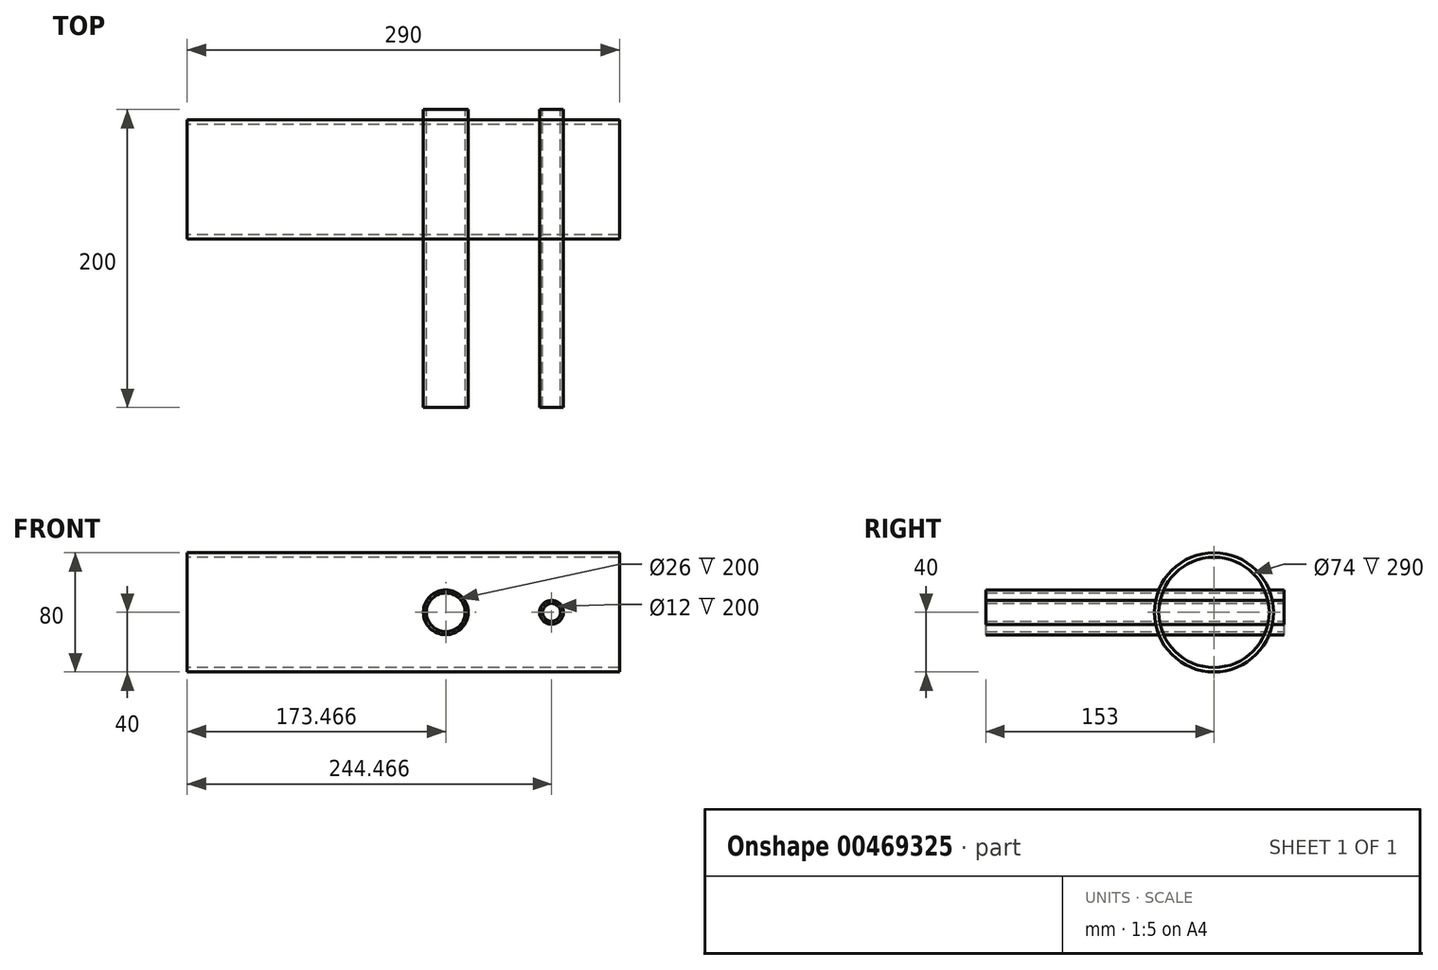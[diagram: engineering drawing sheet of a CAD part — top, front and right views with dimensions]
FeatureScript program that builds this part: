
annotation { "Feature Type Name" : "Feature", "Feature Type Description" : "" }
export const myFeature = defineFeature(function(context is Context, id is Id, definition is map)
    precondition{}
    {
        {
            var Q0;
            Q0=qCreatedBy(makeId("Top.planeOp"),FACE);
            var sketch = newSketch(context, id + "F0", { "sketchPlane" : qUnion([Q0])});
            skLineSegment(sketch, "E0", {"start": v(0.97, -111.55) * mm, "end": v(0.97, 88.45) * mm});
            skLineSegment(sketch, "E1", {"start": v(0.97, 88.45) * mm, "end": v(25.97, 88.45) * mm});
            skLineSegment(sketch, "E2", {"start": v(25.97, 88.45) * mm, "end": v(25.97, -111.55) * mm});
            skLineSegment(sketch, "E3", {"start": v(25.97, -111.55) * mm, "end": v(0.97, -111.55) * mm});
            skLineSegment(sketch, "E4.bottom", {"start": v(79.47, 0) * mm, "end": v(89.47, 0) * mm});
            skLineSegment(sketch, "E4.top", {"start": v(79.47, -46.91) * mm, "end": v(89.47, -46.91) * mm});
            skLineSegment(sketch, "E4.left", {"start": v(79.47, 0) * mm, "end": v(79.47, -46.91) * mm});
            skLineSegment(sketch, "E4.right", {"start": v(89.47, 0) * mm, "end": v(89.47, -46.91) * mm});
            skSolve(sketch);
        }
        {
            var Q0;
            Q0=qCreatedBy(makeId("Front.planeOp"),FACE);
            var sketch = newSketch(context, id + "F1", { "sketchPlane" : qUnion([Q0])});
            skPoint(sketch, "E5", {"position": v(0.97, 0) * mm});
            skPoint(sketch, "E6", {"position": v(25.97, 0) * mm});
            skCircle(sketch, "E7", {"center": v(13.47, 0) * mm, "radius": 13 * mm});
            skCircle(sketch, "E8", {"center": v(84.47, 0) * mm, "radius": 5 * mm, "construction": true});
            skCircle(sketch, "E9", {"center": v(13.47, 0) * mm, "radius": 15 * mm});
            skCircle(sketch, "E10", {"center": v(13.47, 0) * mm, "radius": 12.5 * mm, "construction": true});
            skCircle(sketch, "E11", {"center": v(84.47, 0) * mm, "radius": 6 * mm});
            skCircle(sketch, "E12", {"center": v(84.47, 0) * mm, "radius": 8 * mm});
            skSolve(sketch);
        }
        {
            var Q0;
            Q0=makeQuery(id+"F1.imprint","IMPRINT",FACE,{"disambiguationData":[TD([[makeQuery(id+"F1.imprint","IMPRINT",EDGE,{"derivedFrom":sQuery(id+"F1.wireOp",EDGE,"E7")}),-1.0]])]});
            var Q1;
            Q1=sQuery(id+"F1.wireOp",EDGE,"E9");
            var Q2;
            Q2=sQuery(id+"F1.wireOp",EDGE,"E7");
            extrude(context, id + "F2", {"entities" : qUnion([Q0]), "surfaceEntities" : qUnion([Q1, Q2]), "depth" : 115 * mm, "hasSecondDirection" : true, "secondDirectionOppositeDirection" : true, "secondDirectionDepth" : 85 * mm});
        }
        {
            var Q0;
            Q0=makeQuery(id+"F1.imprint","IMPRINT",FACE,{"disambiguationData":[TD([[makeQuery(id+"F1.imprint","IMPRINT",EDGE,{"derivedFrom":sQuery(id+"F1.wireOp",EDGE,"E11")}),-1.0]])]});
            var Q1;
            Q1=sQuery(id+"F1.wireOp",EDGE,"E12");
            var Q2;
            Q2=sQuery(id+"F1.wireOp",EDGE,"E11");
            var Q3;
            Q3 = qConstructionFilter(qBodyType(qCreatedBy(id + "F4" ,EDGE), BodyType.WIRE), ConstructionObject.NO);
            extrude(context, id + "F3", {"entities" : qUnion([Q0]), "surfaceEntities" : qUnion([Q1, Q2, Q3]), "depth" : 115 * mm, "hasSecondDirection" : true, "secondDirectionOppositeDirection" : true, "secondDirectionDepth" : 85 * mm});
        }
        {
            var Q0;
            Q0=qCreatedBy(makeId("Top.planeOp"),FACE);
            var sketch = newSketch(context, id + "F4", { "sketchPlane" : qUnion([Q0])});
            skPoint(sketch, "E13", {"position": v(0, 38) * mm});
            skPoint(sketch, "E14", {"position": v(0, 85) * mm});
            skLineSegment(sketch, "E15", {"start": v(0, 38) * mm, "end": v(135.55, 38) * mm, "construction": true});
            skLineSegment(sketch, "E16", {"start": v(0, 38) * mm, "end": v(-115.76, 38) * mm, "construction": true});
            skSolve(sketch);
        }
        {
            var Q0;
            Q0=qCreatedBy(makeId("Right.planeOp"),FACE);
            var sketch = newSketch(context, id + "F5", { "sketchPlane" : qUnion([Q0])});
            skCircle(sketch, "E17", {"center": v(38, 0) * mm, "radius": 40 * mm});
            skCircle(sketch, "E18", {"center": v(38, 0) * mm, "radius": 37 * mm});
            skSolve(sketch);
        }
        {
            var Q0;
            Q0 = qSketchRegion(id + "F5", true);
            extrude(context, id + "F6", {"entities" : qUnion([Q0]), "depth" : 130 * mm, "hasSecondDirection" : true, "secondDirectionOppositeDirection" : true, "secondDirectionDepth" : 160 * mm});
        }
    });
